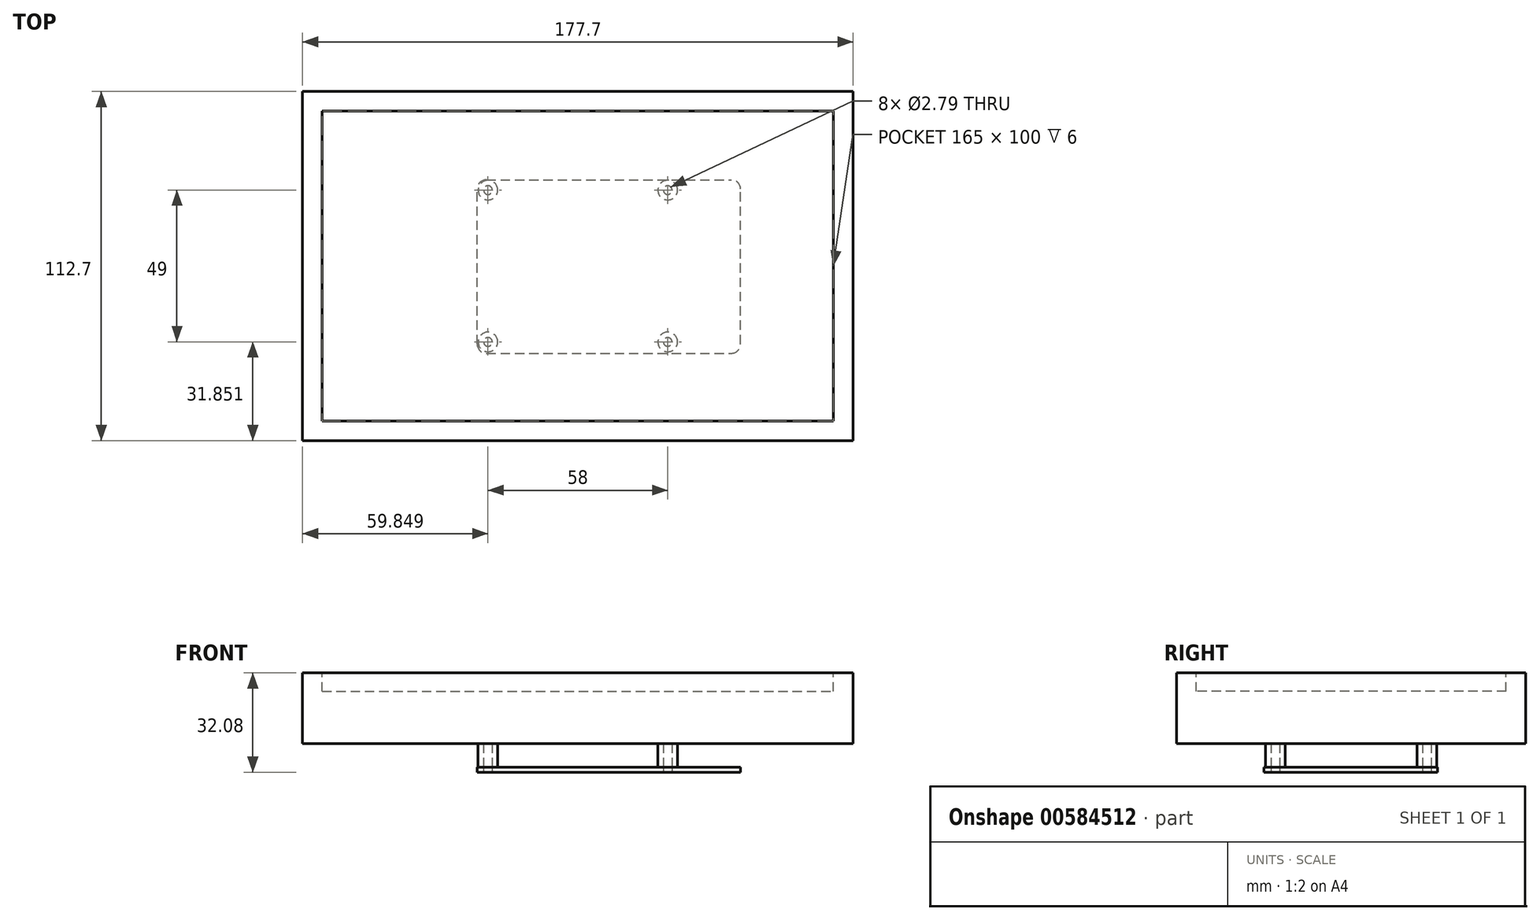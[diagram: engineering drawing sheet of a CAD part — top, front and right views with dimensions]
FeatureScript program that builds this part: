
annotation { "Feature Type Name" : "Feature", "Feature Type Description" : "" }
export const myFeature = defineFeature(function(context is Context, id is Id, definition is map)
    precondition{}
    {
        {
            var Q0;
            Q0=qCreatedBy(makeId("Top.planeOp"),FACE);
            var sketch = newSketch(context, id + "F0", { "sketchPlane" : qUnion([Q0])});
            skLineSegment(sketch, "E0.bottom", {"start": v(-7.27, 42.54) * mm, "end": v(50.73, 42.54) * mm, "construction": true});
            skLineSegment(sketch, "E0.top", {"start": v(-7.27, -6.46) * mm, "end": v(50.73, -6.46) * mm, "construction": true});
            skLineSegment(sketch, "E0.left", {"start": v(-7.27, 42.54) * mm, "end": v(-7.27, -6.46) * mm, "construction": true});
            skLineSegment(sketch, "E0.right", {"start": v(50.73, 42.54) * mm, "end": v(50.73, -6.46) * mm, "construction": true});
            skCircle(sketch, "E1", {"center": v(-7.27, 42.54) * mm, "radius": 1.4 * mm});
            skCircle(sketch, "E2", {"center": v(50.73, 42.54) * mm, "radius": 1.4 * mm});
            skCircle(sketch, "E3", {"center": v(50.73, -6.46) * mm, "radius": 1.4 * mm});
            skCircle(sketch, "E4", {"center": v(-7.27, -6.46) * mm, "radius": 1.4 * mm});
            skLineSegment(sketch, "E5.bottom", {"start": v(-7.77, -10.13) * mm, "end": v(71.23, -10.13) * mm});
            skLineSegment(sketch, "E5.top", {"start": v(-7.77, 45.87) * mm, "end": v(71.23, 45.87) * mm});
            skLineSegment(sketch, "E5.left", {"start": v(-10.77, -7.13) * mm, "end": v(-10.77, 42.87) * mm});
            skLineSegment(sketch, "E5.right", {"start": v(74.23, -7.13) * mm, "end": v(74.23, 42.87) * mm});
            skPoint(sketch, "E6.visualSharp", {"position": v(-10.77, -10.13) * mm});
            skArc(sketch, "E6.filletArc", {"start": v(-10.77, -7.13) * mm, "mid": v(-9.9, -9.25) * mm, "end": v(-7.77, -10.13) * mm});
            skPoint(sketch, "E7.visualSharp", {"position": v(74.23, -10.13) * mm});
            skArc(sketch, "E7.filletArc", {"start": v(71.23, -10.13) * mm, "mid": v(73.35, -9.25) * mm, "end": v(74.23, -7.13) * mm});
            skPoint(sketch, "E8.visualSharp", {"position": v(74.23, 45.87) * mm});
            skArc(sketch, "E8.filletArc", {"start": v(74.23, 42.87) * mm, "mid": v(73.35, 44.99) * mm, "end": v(71.23, 45.87) * mm});
            skPoint(sketch, "E9.visualSharp", {"position": v(-10.77, 45.87) * mm});
            skArc(sketch, "E9.filletArc", {"start": v(-7.77, 45.87) * mm, "mid": v(-9.9, 44.99) * mm, "end": v(-10.77, 42.87) * mm});
            skLineSegment(sketch, "E10", {"start": v(-7.27, 17.87) * mm, "end": v(-10.77, 17.87) * mm});
            skPoint(sketch, "E10.startSnap0", {"position": v(-10.77, 17.87) * mm});
            skSolve(sketch);
        }
        {
            var Q0;
            Q0 = qSketchRegion(id + "F0", true);
            extrude(context, id + "F1", {"entities" : qUnion([Q0]), "depth" : 1.6 * mm, "offsetDistance" : 25.4 * mm});
        }
        {
            var Q0;
            Q0=makeQuery(id+"F1.opExtrude","CAP_FACE",FACE,{"disambiguationData":[OSD([sQuery(id+"F0.wireOp",EDGE,"E1"),sQuery(id+"F0.wireOp",EDGE,"E2"),sQuery(id+"F0.wireOp",EDGE,"E3"),sQuery(id+"F0.wireOp",EDGE,"E4"),sQuery(id+"F0.wireOp",EDGE,"E5.bottom"),sQuery(id+"F0.wireOp",EDGE,"E5.top"),sQuery(id+"F0.wireOp",EDGE,"E5.left"),sQuery(id+"F0.wireOp",EDGE,"E5.right"),sQuery(id+"F0.wireOp",EDGE,"E6.filletArc"),sQuery(id+"F0.wireOp",EDGE,"E7.filletArc"),sQuery(id+"F0.wireOp",EDGE,"E8.filletArc"),sQuery(id+"F0.wireOp",EDGE,"E9.filletArc")])],"isStart":false});
            var sketch = newSketch(context, id + "F2", { "sketchPlane" : qUnion([Q0])});
            skCircle(sketch, "E11", {"center": v(-7.27, 42.54) * mm, "radius": 3.18 * mm});
            skCircle(sketch, "E12", {"center": v(50.73, 42.54) * mm, "radius": 3.18 * mm});
            skCircle(sketch, "E13", {"center": v(50.73, -6.46) * mm, "radius": 3.18 * mm});
            skCircle(sketch, "E14", {"center": v(-7.27, -6.46) * mm, "radius": 3.18 * mm});
            skSolve(sketch);
        }
        {
            var Q0;
            Q0=makeQuery(id+"F2.imprint","IMPRINT",FACE,{"disambiguationData":[TD([[makeQuery(id+"F2.imprint","IMPRINT",EDGE,{"derivedFrom":sQuery(id+"F2.wireOp",EDGE,"E11")}),1.0]])]});
            extrude(context, id + "F3", {"entities" : qUnion([Q0]), "depth" : 7.62 * mm, "offsetDistance" : 25.4 * mm});
        }
        {
            var Q0;
            Q0=makeQuery(id+"F2.imprint","IMPRINT",FACE,{"disambiguationData":[TD([[makeQuery(id+"F2.imprint","IMPRINT",EDGE,{"derivedFrom":sQuery(id+"F2.wireOp",EDGE,"E14")}),1.0]])]});
            extrude(context, id + "F4", {"entities" : qUnion([Q0]), "depth" : 7.62 * mm, "offsetDistance" : 25.4 * mm});
        }
        {
            var Q0;
            Q0=makeQuery(id+"F2.imprint","IMPRINT",FACE,{"disambiguationData":[TD([[makeQuery(id+"F2.imprint","IMPRINT",EDGE,{"derivedFrom":sQuery(id+"F2.wireOp",EDGE,"E12")}),1.0]])]});
            extrude(context, id + "F5", {"entities" : qUnion([Q0]), "depth" : 7.62 * mm, "offsetDistance" : 25.4 * mm});
        }
        {
            var Q0;
            Q0=makeQuery(id+"F2.imprint","IMPRINT",FACE,{"disambiguationData":[TD([[makeQuery(id+"F2.imprint","IMPRINT",EDGE,{"derivedFrom":sQuery(id+"F2.wireOp",EDGE,"E13")}),1.0]])]});
            extrude(context, id + "F6", {"entities" : qUnion([Q0]), "depth" : 7.62 * mm, "offsetDistance" : 25.4 * mm});
        }
        {
            var Q0;
            Q0=makeQuery(id+"F4.opExtrude","CAP_FACE",FACE,{"disambiguationData":[OSD([sQuery(id+"F0.wireOp",EDGE,"E4"),sQuery(id+"F2.wireOp",EDGE,"E14")])],"isStart":false});
            var sketch = newSketch(context, id + "F7", { "sketchPlane" : qUnion([Q0])});
            skLineSegment(sketch, "E15.bottom", {"start": v(-60.77, 68.04) * mm, "end": v(104.23, 68.04) * mm, "construction": true});
            skLineSegment(sketch, "E15.top", {"start": v(-60.77, -31.96) * mm, "end": v(104.23, -31.96) * mm, "construction": true});
            skLineSegment(sketch, "E15.left", {"start": v(-60.77, 68.04) * mm, "end": v(-60.77, -31.96) * mm, "construction": true});
            skLineSegment(sketch, "E15.right", {"start": v(104.23, 68.04) * mm, "end": v(104.23, -31.96) * mm, "construction": true});
            skLineSegment(sketch, "E16", {"start": v(-7.27, 42.54) * mm, "end": v(50.73, -6.46) * mm, "construction": true});
            skLineSegment(sketch, "E17", {"start": v(104.23, 68.04) * mm, "end": v(-60.77, -31.96) * mm, "construction": true});
            skPoint(sketch, "E18", {"position": v(21.73, 18.04) * mm});
            skLineSegment(sketch, "E19.0", {"start": v(-67.12, -38.3) * mm, "end": v(110.58, -38.3) * mm});
            skLineSegment(sketch, "E19.1", {"start": v(-67.12, 74.4) * mm, "end": v(-67.12, -38.3) * mm});
            skLineSegment(sketch, "E19.2", {"start": v(-67.12, 74.4) * mm, "end": v(110.58, 74.4) * mm});
            skLineSegment(sketch, "E19.3", {"start": v(110.58, 74.4) * mm, "end": v(110.58, -38.3) * mm});
            skSolve(sketch);
        }
        {
            var Q0;
            Q0 = qSketchRegion(id + "F7", true);
            extrude(context, id + "F8", {"entities" : qUnion([Q0]), "depth" : 22.86 * mm, "offsetDistance" : 25.4 * mm});
        }
        {
            var Q0;
            Q0=makeQuery(id+"F8.opExtrude","CAP_FACE",FACE,{"disambiguationData":[OSD([sQuery(id+"F7.wireOp",EDGE,"E19.0"),sQuery(id+"F7.wireOp",EDGE,"E19.1"),sQuery(id+"F7.wireOp",EDGE,"E19.2"),sQuery(id+"F7.wireOp",EDGE,"E19.3")])],"isStart":false});
            var sketch = newSketch(context, id + "F9", { "sketchPlane" : qUnion([Q0])});
            skLineSegment(sketch, "E20.0", {"start": v(-60.77, -31.96) * mm, "end": v(104.23, -31.96) * mm});
            skLineSegment(sketch, "E20.1", {"start": v(-60.77, 68.04) * mm, "end": v(-60.77, -31.96) * mm});
            skLineSegment(sketch, "E20.2", {"start": v(-60.77, 68.04) * mm, "end": v(104.23, 68.04) * mm});
            skLineSegment(sketch, "E20.3", {"start": v(104.23, 68.04) * mm, "end": v(104.23, -31.96) * mm});
            skSolve(sketch);
        }
        {
            var Q0;
            Q0 = qSketchRegion(id + "F9", true);
            extrude(context, id + "F10", {"entities" : qUnion([Q0]), "operationType" : NewBodyOperationType.REMOVE, "oppositeDirection" : true, "depth" : 6 * mm, "offsetDistance" : 25.4 * mm});
        }
    });
